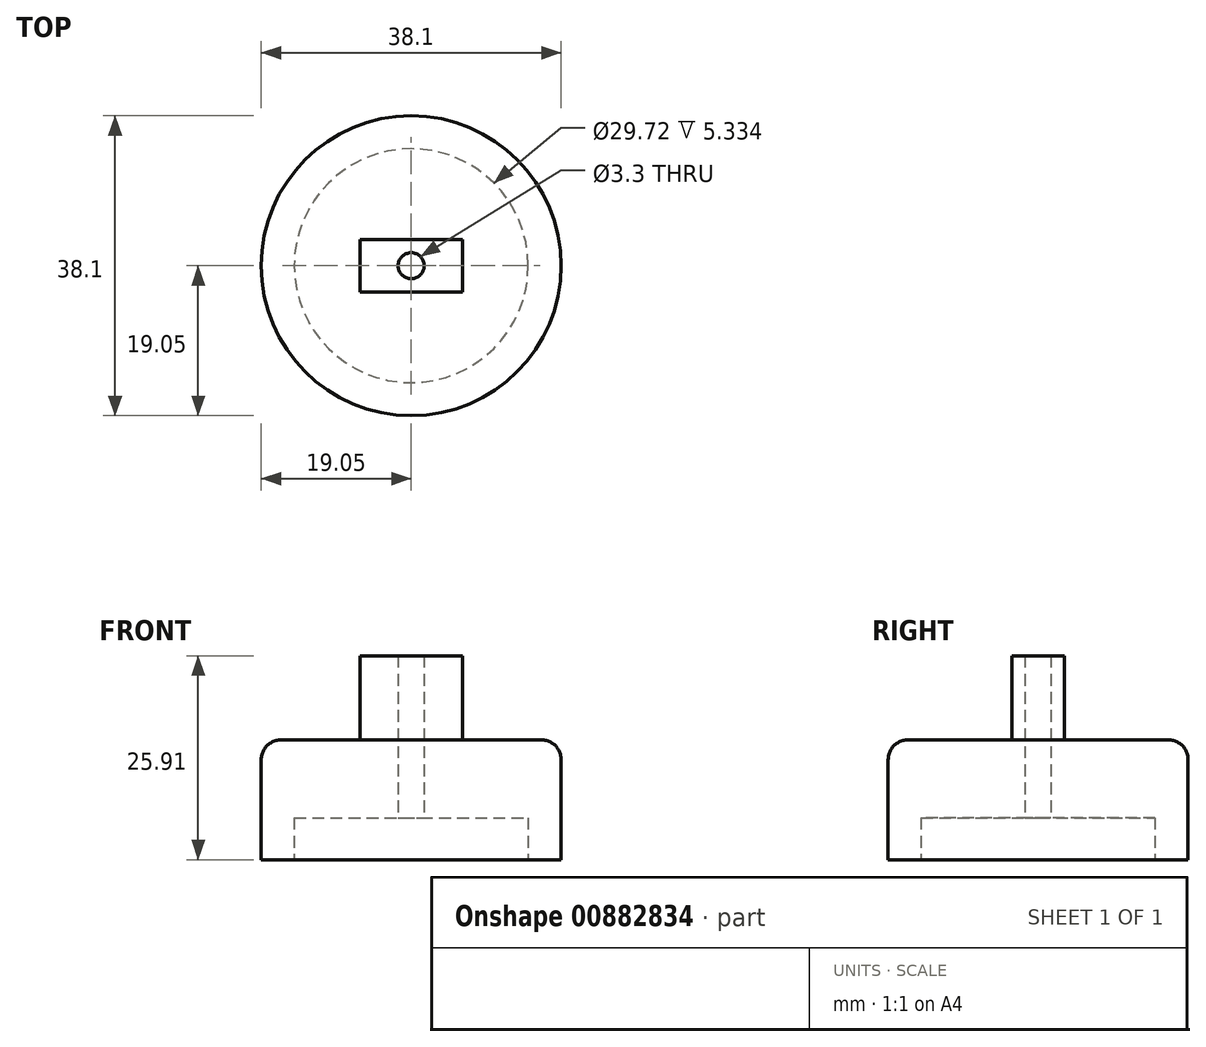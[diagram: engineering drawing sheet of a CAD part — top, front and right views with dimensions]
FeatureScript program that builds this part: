
annotation { "Feature Type Name" : "Feature", "Feature Type Description" : "" }
export const myFeature = defineFeature(function(context is Context, id is Id, definition is map)
    precondition{}
    {
        {
            var Q0;
            Q0=qCreatedBy(makeId("Top.planeOp"),FACE);
            var sketch = newSketch(context, id + "F0", { "sketchPlane" : qUnion([Q0])});
            skLineSegment(sketch, "E0.bottom", {"start": v(-6.5, 3.33) * mm, "end": v(6.5, 3.33) * mm});
            skLineSegment(sketch, "E0.top", {"start": v(-6.5, -3.33) * mm, "end": v(6.5, -3.33) * mm});
            skLineSegment(sketch, "E0.left", {"start": v(-6.5, 3.33) * mm, "end": v(-6.5, -3.33) * mm});
            skLineSegment(sketch, "E0.right", {"start": v(6.5, 3.33) * mm, "end": v(6.5, -3.33) * mm});
            skPoint(sketch, "E0.middle", {"position": v(0, 0) * mm});
            skSolve(sketch);
        }
        {
            var Q0;
            Q0=qSketchRegion(id+"F0",true);
            extrude(context, id + "F1", {"entities" : qUnion([Q0]), "depth" : 10.67 * mm, "offsetDistance" : 25.4 * mm});
        }
        {
            var Q0;
            Q0=makeQuery(id+"F1.opExtrude","CAP_FACE",FACE,{"disambiguationData":[OSD([sQuery(id+"F0.wireOp",EDGE,"E0.bottom"),sQuery(id+"F0.wireOp",EDGE,"E0.top"),sQuery(id+"F0.wireOp",EDGE,"E0.left"),sQuery(id+"F0.wireOp",EDGE,"E0.right")])],"isStart":true});
            var sketch = newSketch(context, id + "F2", { "sketchPlane" : qUnion([Q0])});
            skCircle(sketch, "E1", {"center": v(0, 0) * mm, "radius": 19.05 * mm});
            skSolve(sketch);
        }
        {
            var Q0;
            Q0=qSketchRegion(id+"F2",true);
            extrude(context, id + "F3", {"entities" : qUnion([Q0]), "operationType" : NewBodyOperationType.ADD, "depth" : 15.24 * mm, "offsetDistance" : 25.4 * mm});
        }
        {
            var Q0;
            Q0=makeQuery(id+"F3.opExtrude","CAP_EDGE",EDGE,{"disambiguationData":[OSD([sQuery(id+"F2.wireOp",EDGE,"E1")])],"isStart":true});
            fillet(context, id + "F4", {"entities" : qUnion([Q0]), "radius" : 2.54 * mm, "tangentPropagation" : true, "allowEdgeOverflow" : false});
        }
        {
            var Q0;
            Q0=makeQuery(id+"F3.opExtrude","CAP_FACE",FACE,{"disambiguationData":[OSD([sQuery(id+"F2.wireOp",EDGE,"E1")])],"isStart":false});
            var sketch = newSketch(context, id + "F5", { "sketchPlane" : qUnion([Q0])});
            skCircle(sketch, "E2", {"center": v(0, 0) * mm, "radius": 14.86 * mm});
            skSolve(sketch);
        }
        {
            var Q0;
            Q0=qSketchRegion(id+"F5",true);
            extrude(context, id + "F6", {"entities" : qUnion([Q0]), "operationType" : NewBodyOperationType.REMOVE, "oppositeDirection" : true, "depth" : 5.33 * mm, "offsetDistance" : 25.4 * mm});
        }
        {
            var Q0;
            Q0=makeQuery(id+"F6.boolean.opBoolean","COPY",FACE,{"derivedFrom":makeQuery(id+"F6.opExtrude","CAP_FACE",FACE,{"disambiguationData":[OSD([sQuery(id+"F5.wireOp",EDGE,"E2")])],"isStart":false})});
            var sketch = newSketch(context, id + "F7", { "sketchPlane" : qUnion([Q0])});
            skCircle(sketch, "E3", {"center": v(0, 0) * mm, "radius": 1.65 * mm});
            skSolve(sketch);
        }
        {
            var Q0;
            Q0=qSketchRegion(id+"F7",true);
            extrude(context, id + "F8", {"entities" : qUnion([Q0]), "operationType" : NewBodyOperationType.REMOVE, "oppositeDirection" : true, "depth" : 21.59 * mm, "offsetDistance" : 25.4 * mm});
        }
    });
